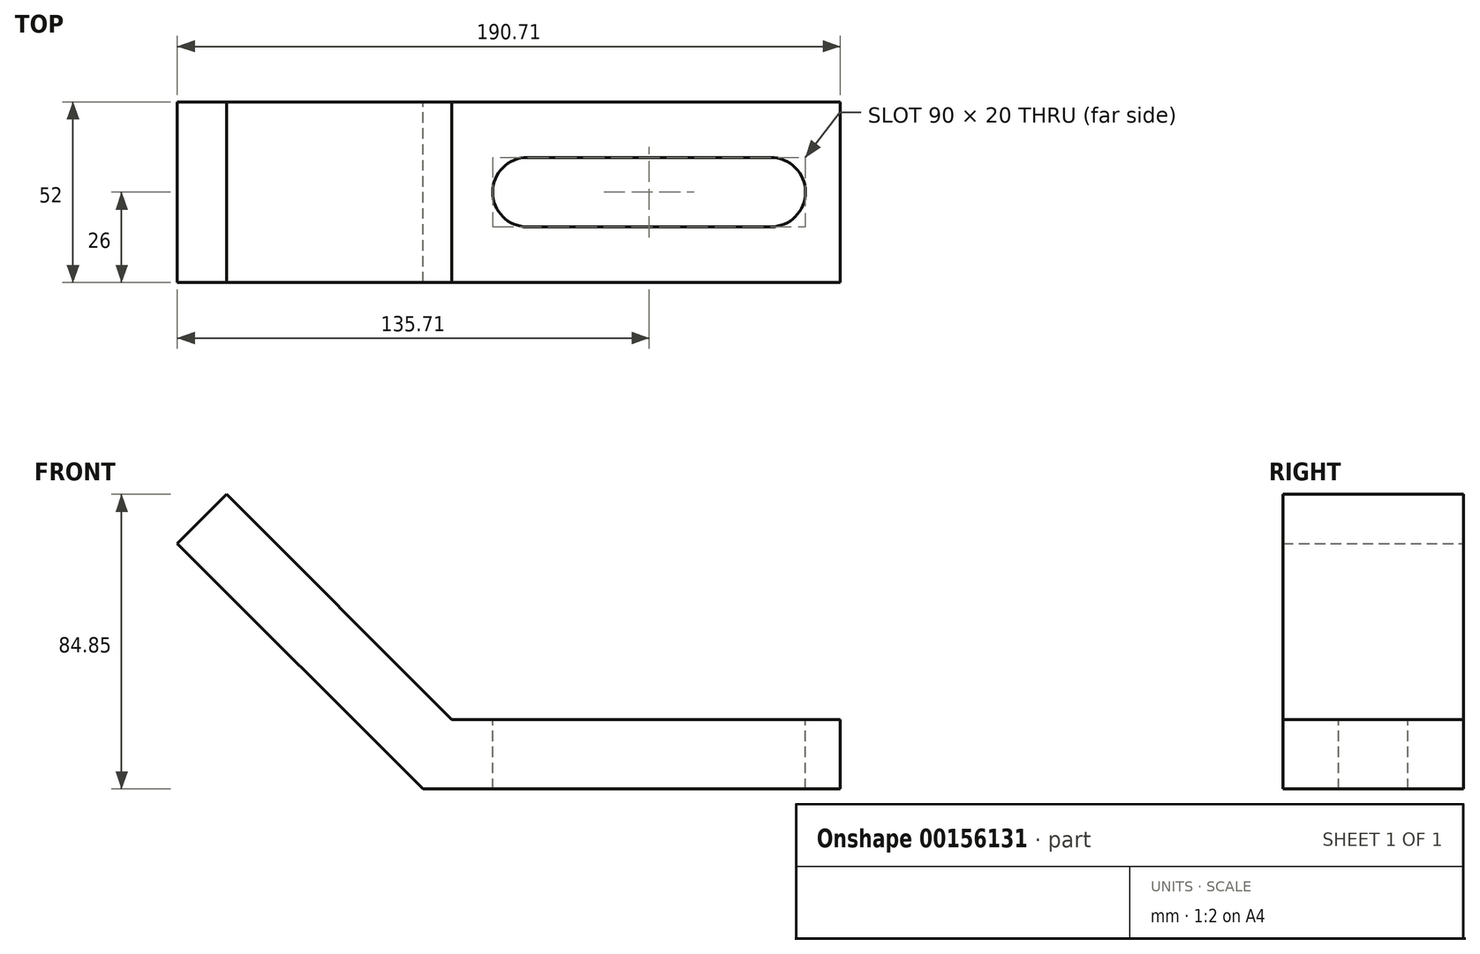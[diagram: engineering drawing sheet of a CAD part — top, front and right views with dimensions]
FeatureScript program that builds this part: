
annotation { "Feature Type Name" : "Feature", "Feature Type Description" : "" }
export const myFeature = defineFeature(function(context is Context, id is Id, definition is map)
    precondition{}
    {
        {
            var Q0;
            Q0=qCreatedBy(makeId("Front.planeOp"),FACE);
            var sketch = newSketch(context, id + "F0", { "sketchPlane" : qUnion([Q0])});
            skLineSegment(sketch, "E0.bottom", {"start": v(0, 0) * mm, "end": v(120, 0) * mm});
            skLineSegment(sketch, "E0.top", {"start": v(8.28, 20) * mm, "end": v(120, 20) * mm});
            skLineSegment(sketch, "E0.left", {"start": v(0, 0) * mm, "end": v(8.28, 20) * mm});
            skLineSegment(sketch, "E0.right", {"start": v(120, 0) * mm, "end": v(120, 20) * mm});
            skLineSegment(sketch, "E1", {"start": v(0, 0) * mm, "end": v(-70.71, 70.71) * mm});
            skLineSegment(sketch, "E2", {"start": v(8.28, 20) * mm, "end": v(-56.57, 84.85) * mm});
            skLineSegment(sketch, "E3", {"start": v(-56.57, 84.85) * mm, "end": v(-70.71, 70.71) * mm});
            skSolve(sketch);
        }
        {
            var Q0;
            Q0 = qSketchRegion(id + "F0", true);
            extrude(context, id + "F1", {"entities" : qUnion([Q0]), "endBound" : BoundingType.SYMMETRIC, "depth" : 52 * mm});
        }
        {
            var Q0;
            Q0=makeQuery(id+"F1.opExtrude","SWEPT_FACE",FACE,{"disambiguationData":[OSD([sQuery(id+"F0.wireOp",EDGE,"E0.top")])]});
            var sketch = newSketch(context, id + "F2", { "sketchPlane" : qUnion([Q0])});
            skLineSegment(sketch, "E4.bottom", {"start": v(100, 10) * mm, "end": v(30, 10) * mm});
            skLineSegment(sketch, "E4.top", {"start": v(100, -10) * mm, "end": v(30, -10) * mm});
            skPoint(sketch, "E4.middle", {"position": v(64.14, 0) * mm});
            skPoint(sketch, "E4.middle.positionSnap0", {"position": v(64.14, -26) * mm});
            skPoint(sketch, "E4.centerSnap0", {"position": v(64.14, -26) * mm});
            skArc(sketch, "E5", {"start": v(30, 10) * mm, "mid": v(20, 0) * mm, "end": v(30, -10) * mm});
            skArc(sketch, "E6", {"start": v(100, 10) * mm, "mid": v(110, 0) * mm, "end": v(100, -10) * mm});
            skPoint(sketch, "E7", {"position": v(20, 0) * mm});
            skPoint(sketch, "E8", {"position": v(110, 0) * mm});
            skSolve(sketch);
        }
        {
            var Q0;
            Q0 = qSketchRegion(id + "F2", true);
            var Q1;
            Q1=makeQuery(id+"F1.opExtrude","SWEPT_FACE",FACE,{"disambiguationData":[OSD([sQuery(id+"F0.wireOp",EDGE,"E0.bottom")])]});
            extrude(context, id + "F3", {"entities" : qUnion([Q0]), "operationType" : NewBodyOperationType.REMOVE, "endBound" : BoundingType.UP_TO_SURFACE, "oppositeDirection" : true, "endBoundEntityFace" : qUnion([Q1]), "depth" : 25.4 * mm});
        }
        {
            var Q0;
            Q0=makeQuery(id+"F1.opExtrude","SWEPT_FACE",FACE,{"disambiguationData":[OSD([sQuery(id+"F0.wireOp",EDGE,"E2")])]});
            var sketch = newSketch(context, id + "F4", { "sketchPlane" : qUnion([Q0])});
            skCircle(sketch, "E9", {"center": v(-74, 0) * mm, "radius": 10 * mm});
            skPoint(sketch, "E9.centerSnap0", {"position": v(-100, 0) * mm});
            skPoint(sketch, "E10", {"position": v(-84, 0) * mm});
            skArc(sketch, "E11", {"start": v(-74, 26) * mm, "mid": v(-100, 0) * mm, "end": v(-74, -26) * mm});
            skSolve(sketch);
        }
        {
            var Q0;
            Q0 = qSketchRegion(id + "F4", true);
            var Q1;
            {var subQ0=sQuery(id+"F4.wireOp",EDGE,"E11");var subQ1=sQuery(id+"F0.wireOp",EDGE,"E2");var subQ2=makeQuery(id+"F1.opExtrude","CAP_EDGE",EDGE,{"disambiguationData":[OSD([subQ1])],"isStart":true});var subQ3=makeQuery(id+"F4.imprint","INTERSECT",VERTEX,{"derivedFrom":[subQ2,subQ0]});Q1=makeQuery(id+"F4.imprint","IMPRINT",FACE,{"disambiguationData":[TD([[makeQuery(id+"F4.imprint","IMPRINT",EDGE,{"disambiguationData":[TD([[subQ3,-1.0]])],"derivedFrom":subQ0}),-1.0]])]});}
            var Q2;
            {var subQ0=sQuery(id+"F4.wireOp",EDGE,"E11");var subQ1=sQuery(id+"F0.wireOp",EDGE,"E2");var subQ2=makeQuery(id+"F1.opExtrude","CAP_EDGE",EDGE,{"disambiguationData":[OSD([subQ1])],"isStart":false});var subQ3=makeQuery(id+"F4.imprint","INTERSECT",VERTEX,{"derivedFrom":[subQ2,subQ0]});Q2=makeQuery(id+"F4.imprint","IMPRINT",FACE,{"disambiguationData":[TD([[makeQuery(id+"F4.imprint","IMPRINT",EDGE,{"disambiguationData":[TD([[subQ3,1.0]])],"derivedFrom":subQ0}),-1.0]])]});}
            var Q3;
            Q3=makeQuery(id+"F1.opExtrude","SWEPT_FACE",FACE,{"disambiguationData":[OSD([sQuery(id+"F0.wireOp",EDGE,"E1")])]});
            extrude(context, id + "F5", {"entities" : qUnion([Q0, Q1, Q2]), "operationType" : NewBodyOperationType.REMOVE, "endBound" : BoundingType.UP_TO_SURFACE, "oppositeDirection" : true, "endBoundEntityFace" : qUnion([Q3]), "depth" : 25 * mm});
        }
    });
